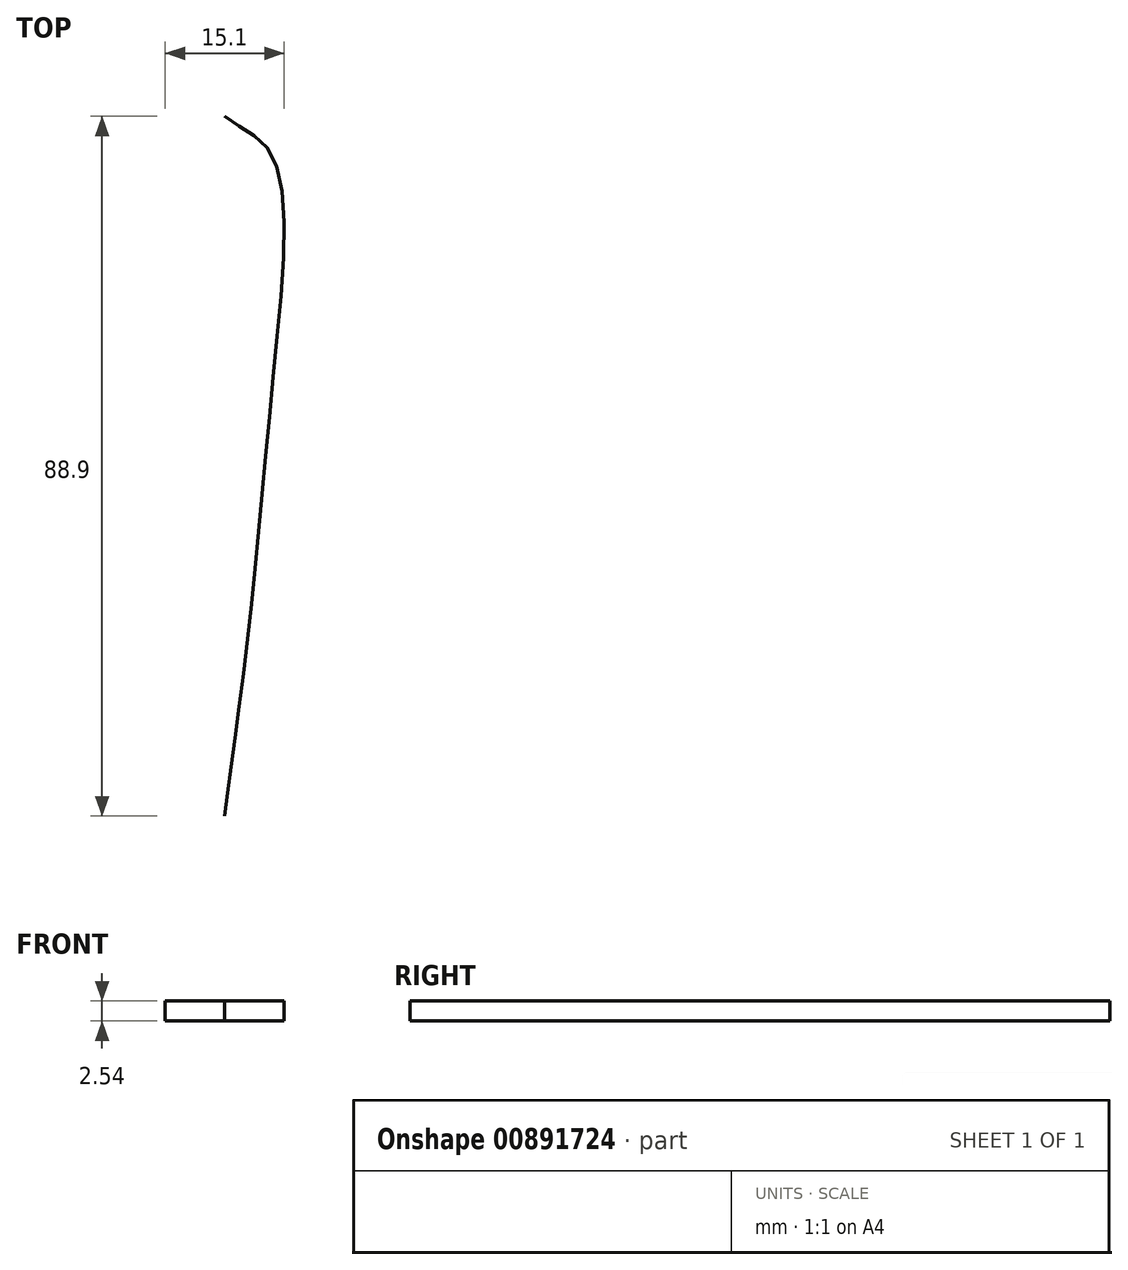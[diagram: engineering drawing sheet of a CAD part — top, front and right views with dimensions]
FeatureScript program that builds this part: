
annotation { "Feature Type Name" : "Feature", "Feature Type Description" : "" }
export const myFeature = defineFeature(function(context is Context, id is Id, definition is map)
    precondition{}
    {
        {
            var Q0;
            Q0=qCreatedBy(makeId("Top.planeOp"),FACE);
            var sketch = newSketch(context, id + "F0", { "sketchPlane" : qUnion([Q0])});
            skFitSpline(sketch, "E0", {"points": [v(0, 27.94) * mm, v(5.99, 23.05) * mm, v(6.18, -5.14) * mm, v(2.8, -39.73) * mm, v(0, -60.96) * mm], "startDerivative": vector(40.92, -32.73) * mm, "endDerivative": vector(-7.17, -61.7) * mm});
            skFitSpline(sketch, "E1.MirrorCS", {"points": [v(0, 27.94) * mm, v(-5.99, 23.05) * mm, v(-6.18, -5.14) * mm, v(-2.8, -39.73) * mm, v(0, -60.96) * mm], "startDerivative": vector(-40.92, -32.73) * mm, "endDerivative": vector(7.17, -61.7) * mm});
            skSolve(sketch);
        }
        {
            var Q0;
            Q0=makeQuery(id+"F0.imprint","IMPRINT",FACE,{"disambiguationData":[TD([[makeQuery(id+"F0.imprint","IMPRINT",EDGE,{"derivedFrom":sQuery(id+"F0.wireOp",EDGE,"E0")}),-1.0]])]});
            extrude(context, id + "F1", {"entities" : qUnion([Q0]), "depth" : 2.54 * mm, "offsetDistance" : 25.4 * mm});
        }
    });
